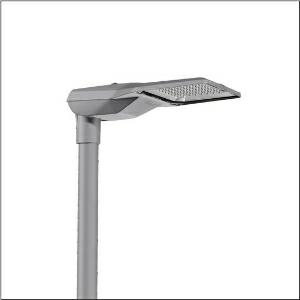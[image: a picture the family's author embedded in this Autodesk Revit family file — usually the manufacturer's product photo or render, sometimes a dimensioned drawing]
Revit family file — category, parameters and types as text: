
# Revit family: streetlight_sl_21_midi___p0_8ab_5xe3r33s08mb_a55a
name_source: partatom
category: Lighting Fixtures
units: mm (PartAtom-declared; Revit-internal decimal feet)

## family parameters
Cut with Voids When Loaded = No
Host = Face
Light Source = No
Part Type = Normal
Room Calculation Point = No
Round Connector Dimension = Use Diameter
Shared = No

## types (1)
- --- (1 x LED, 15870 lm, 136 W, 3000K)
    Apparent Load = 136 VA
    CIE Flux Codes = 36 71 98 100 100
    Color Rendering = 70
    Color Temperature = 3000K
    Default Elevation = 1800 mm
    Description = Streetlight SL 21 midi, mast luminaire, primary light control with lens, of PMMA, primary optical cover: cover, of toughened safety glass, transparent, light distribution: P0.8aB, light emission: direct distribution, primary light characteristic: asymmetric, installation type: post-top, side-entry, LED, High Power LED, rated luminous flux: 15.870lm, luminous efficacy: 117lm/W, light colour: 730, colour temperature: 3000K, control gear: D4i, control: pre-setting: logarithmic dimming characteristic, flexible luminous flux parameterisation, time-dependent luminous flux control, constant luminous flux control, overheat protection, mains connection: 230..240V, AC, 50/60Hz, start of lifetime: 136W, end of service life: 142W, reduction: 61W, luminaire housing, of diecast aluminium, powder-coated, SITECO metallic grey (DB 702S), corrosivity category C5 high according to DIN EN ISO 12944, multi-level sealing system, sealing non-destructively replaceable, inclination adjustable: 0°, 5°, 10°, 15°, please order mast flange separately, length: 644mm, width: 335mm, height: 110mm, mast flange for spigot size: 42mm (side-entry): 5XC10008XM4, 60/48mm (side-entry/post-top): 5XC10108XM2, 76/60mm (side-entry/post-top): 5XC10108XM1, mounting height: 4..8m, Smart Interface above, protection rating (complete): IP66, insulation class (complete): insulation class II (safety insulation), certification: CE, ENEC, ENEC+, VDE, impact resistance: IK10, permissible operating ambient temperature for outdoor applications: -40..+50°C, standard-compliant lighting for roads and squares, packaging unit: 1 piece

Light Distribution: P0.8aB
    Height = 111 mm
    Lamp = 1 x LED
    Lamp Light Flux = 15870 lm
    Lamp Power = 136 W
    Lamp count = 1
    Length = 644 mm
    Luminous efficacy = 117 lm/W
    Manufacturer = Siteco
    ModVariant = No
    Model = 5XE3R33S08MB
    Number of Poles = 1
    OnlyDefault = Yes
    Power Factor = 1
    Product Name = Streetlight SL 21 midi | P0.8aB
    Product group = mast luminaire | pylon top
    ProductGroupID = 6100
    Protection Class = Protection class II
    Protection Degree = IP 66
    RLX_Detail_Level = 1
    RLX_Emergency_Light_Flux = 0 lm
    RLX_Emergency_Type = 0
    RLX_Emergency_Type_DB = No
    RlxData = <blob elided: 90065 chars, md5=0ac42c34>
    Socket = socket
    Standby Power = 0 W
    System Light Flux = 15870 lm
    System Power = 136 W
    Type Comments = factory setting: luminous flux: 100 % | dim-lin: 254 | 695 mA
    Type Image = l_1004302.jpg
    URL = http://relux.com
    VarID = @adj_082747
    Voltage = 0 V
    Weight = 0.00 kg
    Width = 336 mm

## geometry (parser evidence)
native form markers: Blend x4, Sweep x10
no freeform markers — native parametric forms only
